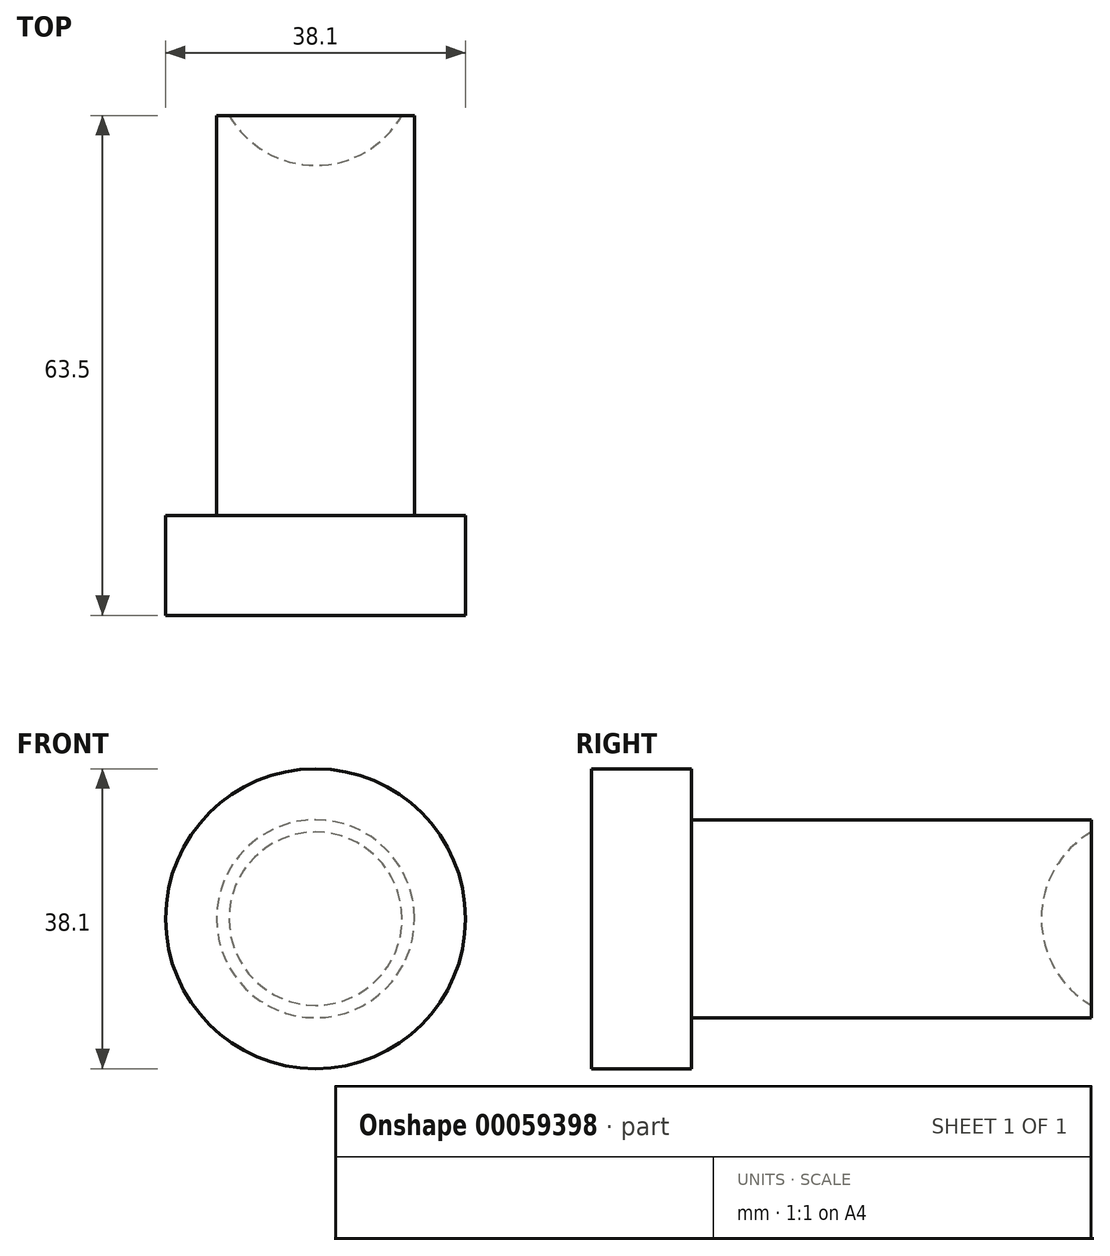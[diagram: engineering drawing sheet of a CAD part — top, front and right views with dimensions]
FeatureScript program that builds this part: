
annotation { "Feature Type Name" : "Feature", "Feature Type Description" : "" }
export const myFeature = defineFeature(function(context is Context, id is Id, definition is map)
    precondition{}
    {
        {
            var Q0;
            Q0=qCreatedBy(makeId("Front.planeOp"),FACE);
            var sketch = newSketch(context, id + "F0", { "sketchPlane" : qUnion([Q0])});
            skCircle(sketch, "E0", {"center": v(0, 0) * mm, "radius": 19.05 * mm});
            skSolve(sketch);
        }
        {
            var Q0;
            Q0 = qSketchRegion(id + "F0", true);
            extrude(context, id + "F1", {"entities" : qUnion([Q0]), "oppositeDirection" : true, "depth" : 12.7 * mm});
        }
        {
            var Q0;
            Q0=makeQuery(id+"F1.opExtrude","CAP_FACE",FACE,{"disambiguationData":[OSD([sQuery(id+"F0.wireOp",EDGE,"E0")])],"isStart":false});
            var sketch = newSketch(context, id + "F2", { "sketchPlane" : qUnion([Q0])});
            skCircle(sketch, "E1", {"center": v(0, 0) * mm, "radius": 12.57 * mm});
            skSolve(sketch);
        }
        {
            var Q0;
            Q0 = qSketchRegion(id + "F2", true);
            extrude(context, id + "F3", {"entities" : qUnion([Q0]), "operationType" : NewBodyOperationType.ADD, "depth" : 50.8 * mm});
        }
        {
            var Q0;
            Q0=qCreatedBy(makeId("Front.planeOp"),FACE);
            cPlane(context, id + "F4", {"entities" : qUnion([Q0]), "cplaneType" : CPlaneType.OFFSET, "offset" : 69.85 * mm, "oppositeDirection" : true, "width" : 152.4 * mm, "height" : 152.4 * mm});
        }
        {
            var Q0;
            Q0=qCreatedBy(id+"F4.planeOp",FACE);
            var sketch = newSketch(context, id + "F5", { "sketchPlane" : qUnion([Q0])});
            skLineSegment(sketch, "E2", {"start": v(20.4, 0) * mm, "end": v(-24.5, 0) * mm});
            skArc(sketch, "E3", {"start": v(12.7, 0) * mm, "mid": v(0, 12.7) * mm, "end": v(-12.7, 0) * mm});
            skLineSegment(sketch, "E4", {"start": v(12.7, 0) * mm, "end": v(-12.7, 0) * mm});
            skSolve(sketch);
        }
        {
            var Q0;
            Q0 = qSketchRegion(id + "F5", true);
            var Q1;
            Q1=sQuery(id+"F5.wireOp",EDGE,"E2");
            revolve(context, id + "F6", {"operationType" : NewBodyOperationType.REMOVE, "entities" : qUnion([Q0]), "axis" : qUnion([Q1]), "revolveType" : RevolveType.FULL, "oppositeDirection" : true});
        }
    });
